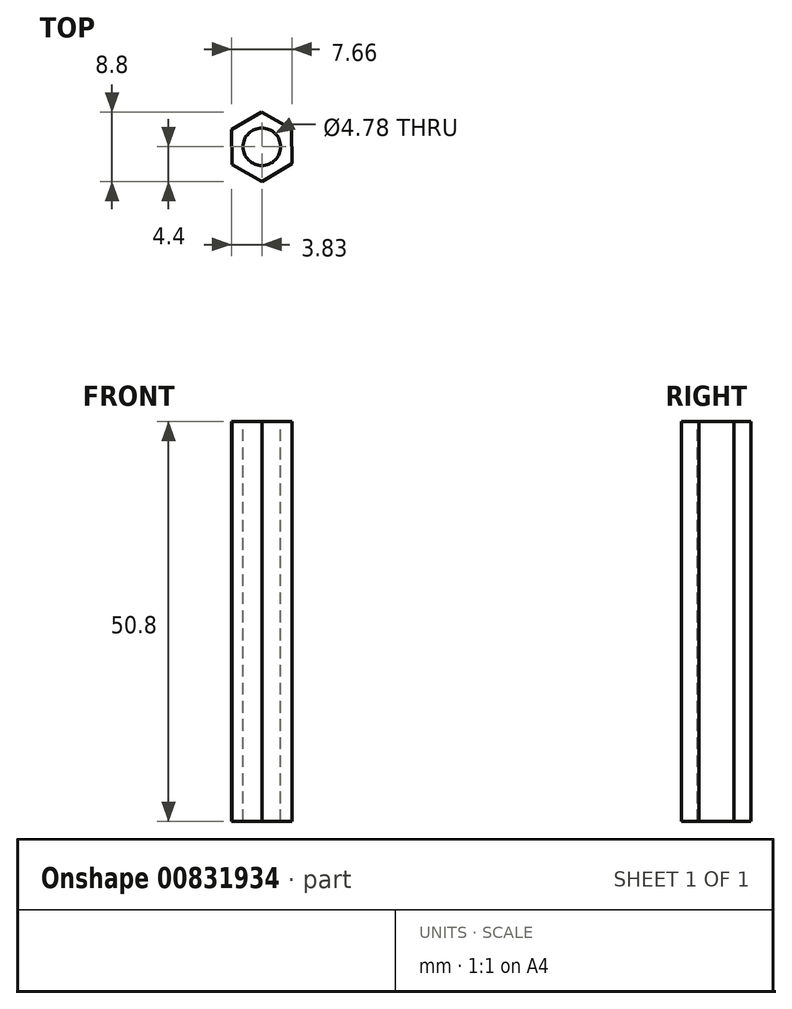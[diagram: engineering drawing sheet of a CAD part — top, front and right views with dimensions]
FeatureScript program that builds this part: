
annotation { "Feature Type Name" : "Feature", "Feature Type Description" : "" }
export const myFeature = defineFeature(function(context is Context, id is Id, definition is map)
    precondition{}
    {
        {
            var Q0;
            Q0=qCreatedBy(makeId("Top.planeOp"),FACE);
            var sketch = newSketch(context, id + "F0", { "sketchPlane" : qUnion([Q0])});
            skCircle(sketch, "E0.cCircle", {"center": v(0, 0) * mm, "radius": 3.8 * mm, "construction": true});
            skLineSegment(sketch, "E0.0", {"start": v(-0.05, 4.4) * mm, "end": v(3.79, 2.24) * mm});
            skLineSegment(sketch, "E0.1", {"start": v(3.79, 2.24) * mm, "end": v(3.83, -2.16) * mm});
            skLineSegment(sketch, "E0.2", {"start": v(3.83, -2.16) * mm, "end": v(0.05, -4.4) * mm});
            skLineSegment(sketch, "E0.3", {"start": v(0.05, -4.4) * mm, "end": v(-3.79, -2.24) * mm});
            skLineSegment(sketch, "E0.4", {"start": v(-3.79, -2.24) * mm, "end": v(-3.83, 2.16) * mm});
            skLineSegment(sketch, "E0.5", {"start": v(-3.83, 2.16) * mm, "end": v(-0.05, 4.4) * mm});
            skPoint(sketch, "E0.0.midPoint", {"position": v(1.87, 3.32) * mm});
            skSolve(sketch);
        }
        {
            var Q0;
            Q0=makeQuery(id+"F0.imprint","IMPRINT",FACE,{"disambiguationData":[TD([[makeQuery(id+"F0.imprint","IMPRINT",EDGE,{"derivedFrom":sQuery(id+"F0.wireOp",EDGE,"E0.0")}),-1.0]])]});
            extrude(context, id + "F1", {"entities" : qUnion([Q0]), "depth" : 50.8 * mm, "offsetDistance" : 25.4 * mm});
        }
        {
            var Q0;
            Q0=makeQuery(id+"F1.opExtrude","CAP_FACE",FACE,{"disambiguationData":[OSD([sQuery(id+"F0.wireOp",EDGE,"E0.0"),sQuery(id+"F0.wireOp",EDGE,"E0.1"),sQuery(id+"F0.wireOp",EDGE,"E0.2"),sQuery(id+"F0.wireOp",EDGE,"E0.3"),sQuery(id+"F0.wireOp",EDGE,"E0.4"),sQuery(id+"F0.wireOp",EDGE,"E0.5")])],"isStart":false});
            var sketch = newSketch(context, id + "F2", { "sketchPlane" : qUnion([Q0])});
            skCircle(sketch, "E1", {"center": v(0, 0) * mm, "radius": 2.39 * mm});
            skSolve(sketch);
        }
        {
            var Q0;
            Q0=qSketchRegion(id+"F2",true);
            extrude(context, id + "F3", {"entities" : qUnion([Q0]), "operationType" : NewBodyOperationType.REMOVE, "oppositeDirection" : true, "depth" : 50.8 * mm, "offsetDistance" : 25.4 * mm});
        }
    });
